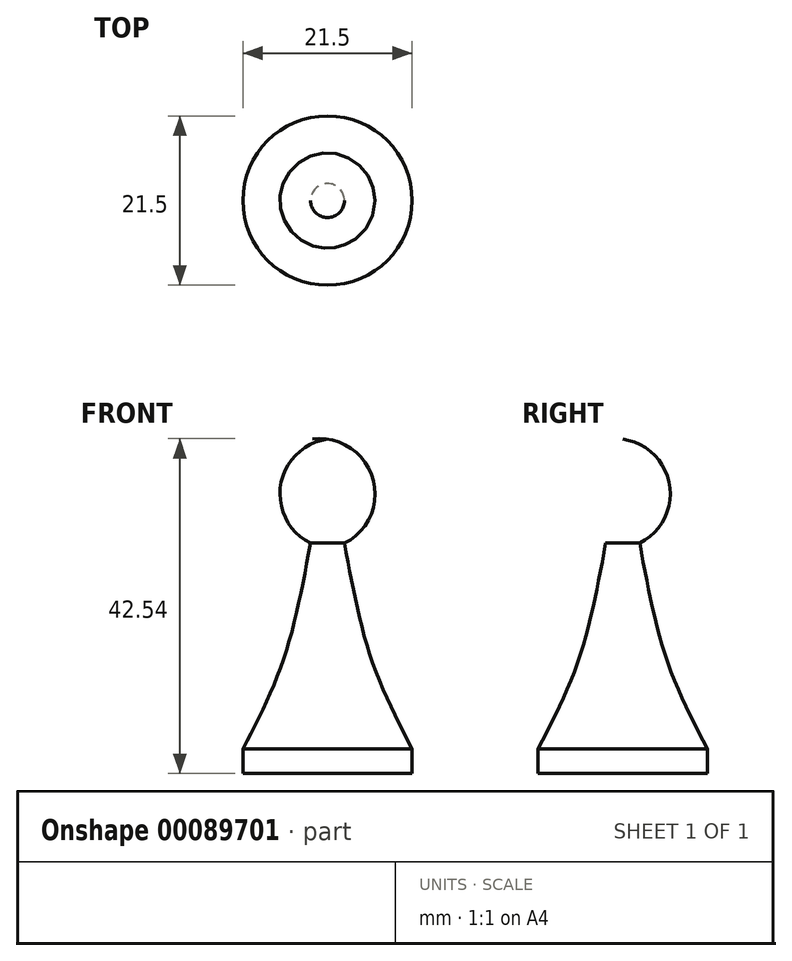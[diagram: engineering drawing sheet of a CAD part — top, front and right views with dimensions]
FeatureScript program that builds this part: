
annotation { "Feature Type Name" : "Feature", "Feature Type Description" : "" }
export const myFeature = defineFeature(function(context is Context, id is Id, definition is map)
    precondition{}
    {
        {
            var Q0;
            Q0=qCreatedBy(makeId("Front.planeOp"),FACE);
            var sketch = newSketch(context, id + "F0", { "sketchPlane" : qUnion([Q0])});
            skArc(sketch, "E0", {"start": v(0, 42.47) * mm, "mid": v(-6.04, 35.54) * mm, "end": v(0, 28.6) * mm});
            skLineSegment(sketch, "E1", {"start": v(-10.75, 3.14) * mm, "end": v(-10.75, 0) * mm});
            skLineSegment(sketch, "E2", {"start": v(-10.75, 0) * mm, "end": v(0, 0) * mm});
            skLineSegment(sketch, "E3", {"start": v(0, 0) * mm, "end": v(0, 42.47) * mm});
            skFitSpline(sketch, "E4", {"points": [v(-2.16, 29.27) * mm, v(-5.61, 14.42) * mm, v(-10.75, 3.14) * mm], "startDerivative": vector(-5.44, -29.4) * mm, "endDerivative": vector(-11.83, -22.73) * mm});
            skSolve(sketch);
        }
        {
            var Q0;
            {var subQ0=sQuery(id+"F0.wireOp",EDGE,"E3");var subQ1=sQuery(id+"F0.wireOp",EDGE,"E0");var subQ2=makeQuery(id+"F0.imprint","INTERSECT",VERTEX,{"disambiguationData":[OD(0.0)],"derivedFrom":[subQ1,subQ0]});Q0=makeQuery(id+"F0.imprint","IMPRINT",FACE,{"disambiguationData":[TD([[makeQuery(id+"F0.imprint","IMPRINT",EDGE,{"disambiguationData":[TD([[subQ2,-1.0]])],"derivedFrom":subQ1}),1.0]])]});}
            var Q1;
            Q1=makeQuery(id+"F0.imprint","IMPRINT",FACE,{"disambiguationData":[TD([[makeQuery(id+"F0.imprint","IMPRINT",EDGE,{"derivedFrom":sQuery(id+"F0.wireOp",EDGE,"E1")}),1.0]])]});
            var Q2;
            Q2=sQuery(id+"F0.wireOp",EDGE,"E3");
            revolve(context, id + "F1", {"entities" : qUnion([Q0, Q1]), "axis" : qUnion([Q2]), "revolveType" : RevolveType.FULL});
        }
    });
